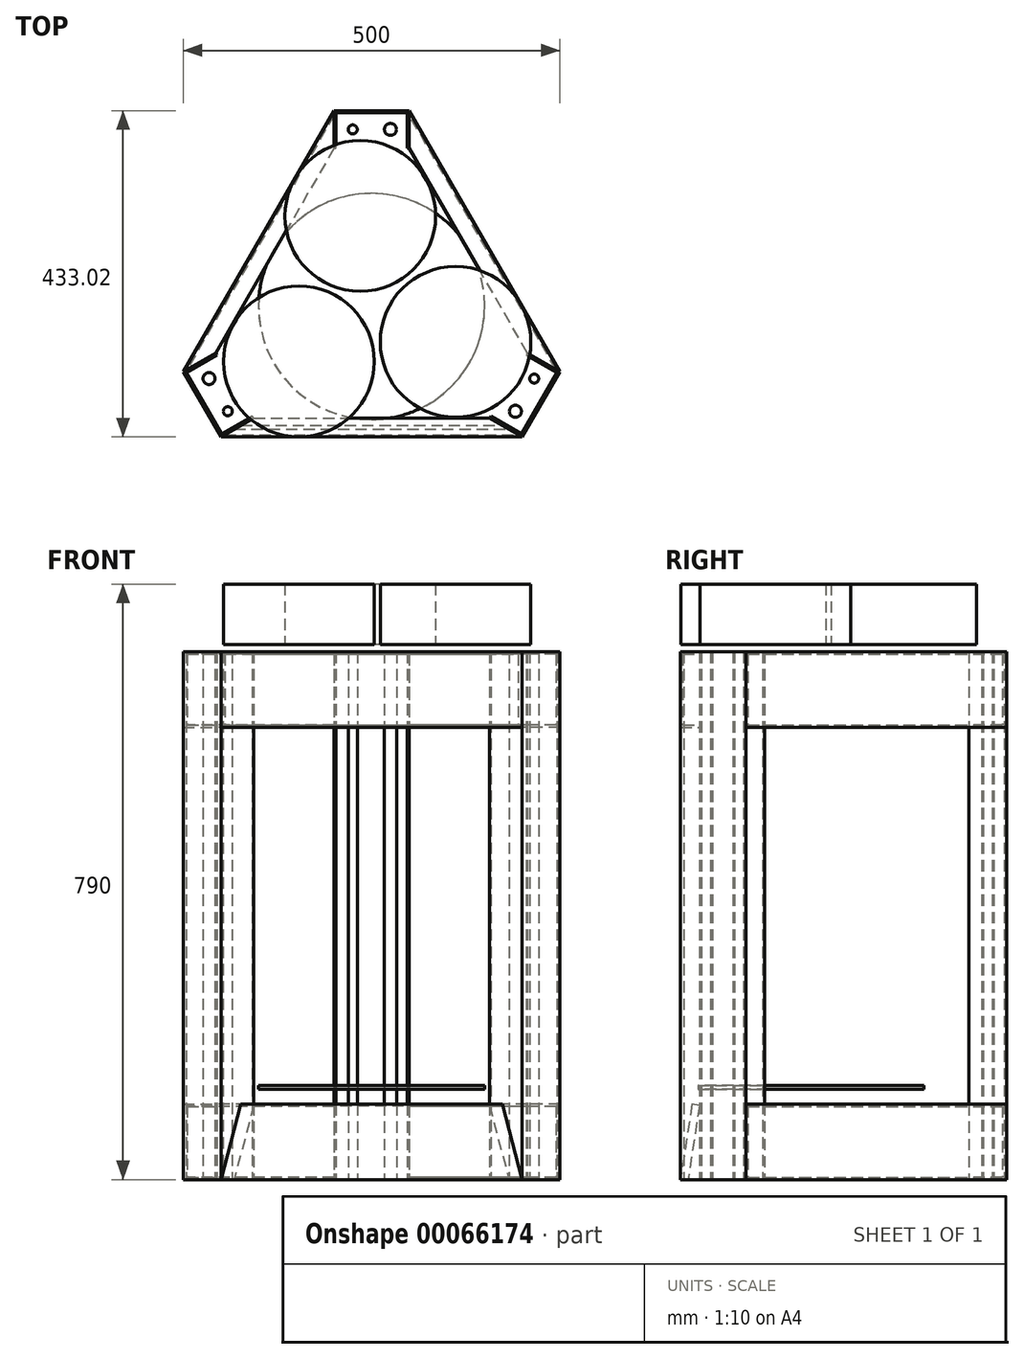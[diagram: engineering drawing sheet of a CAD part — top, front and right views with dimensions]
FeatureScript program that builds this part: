
annotation { "Feature Type Name" : "Feature", "Feature Type Description" : "" }
export const myFeature = defineFeature(function(context is Context, id is Id, definition is map)
    precondition{}
    {
        {
            var Q0;
            Q0=qCreatedBy(makeId("Top.planeOp"),FACE);
            var sketch = newSketch(context, id + "F0", { "sketchPlane" : qUnion([Q0])});
            skLineSegment(sketch, "E0.bottom", {"start": v(-50, 209.8) * mm, "end": v(50, 209.8) * mm});
            skLineSegment(sketch, "E0.top", {"start": v(-50, 259.8) * mm, "end": v(50, 259.8) * mm});
            skLineSegment(sketch, "E0.left", {"start": v(-50, 209.8) * mm, "end": v(-50, 259.8) * mm});
            skLineSegment(sketch, "E0.right", {"start": v(50, 209.8) * mm, "end": v(50, 259.8) * mm});
            skPoint(sketch, "E0.middle", {"position": v(0, 234.8) * mm});
            skLineSegment(sketch, "E1.0", {"start": v(47, 209.8) * mm, "end": v(47, 256.8) * mm});
            skLineSegment(sketch, "E1.1", {"start": v(-47, 256.8) * mm, "end": v(47, 256.8) * mm});
            skLineSegment(sketch, "E1.2", {"start": v(-47, 209.8) * mm, "end": v(-47, 256.8) * mm});
            skLineSegment(sketch, "E2.1.0", {"start": v(-198.9, -169.1) * mm, "end": v(-245.9, -87.7) * mm});
            skLineSegment(sketch, "E2.1.1", {"start": v(-200, -173.2) * mm, "end": v(-250, -86.6) * mm});
            skLineSegment(sketch, "E2.1.2", {"start": v(-156.7, -148.2) * mm, "end": v(-200, -173.2) * mm});
            skLineSegment(sketch, "E2.1.3", {"start": v(-158.2, -145.6) * mm, "end": v(-198.9, -169.1) * mm});
            skLineSegment(sketch, "E2.1.4", {"start": v(-205.2, -64.2) * mm, "end": v(-245.9, -87.7) * mm});
            skLineSegment(sketch, "E2.1.5", {"start": v(-206.7, -61.6) * mm, "end": v(-250, -86.6) * mm});
            skLineSegment(sketch, "E2.1.6", {"start": v(-156.7, -148.2) * mm, "end": v(-206.7, -61.6) * mm});
            skLineSegment(sketch, "E2.2.0", {"start": v(245.9, -87.7) * mm, "end": v(198.9, -169.1) * mm});
            skLineSegment(sketch, "E2.2.1", {"start": v(250, -86.6) * mm, "end": v(200, -173.2) * mm});
            skLineSegment(sketch, "E2.2.2", {"start": v(206.7, -61.6) * mm, "end": v(250, -86.6) * mm});
            skLineSegment(sketch, "E2.2.3", {"start": v(205.2, -64.2) * mm, "end": v(245.9, -87.7) * mm});
            skLineSegment(sketch, "E2.2.4", {"start": v(158.2, -145.6) * mm, "end": v(198.9, -169.1) * mm});
            skLineSegment(sketch, "E2.2.5", {"start": v(156.7, -148.2) * mm, "end": v(200, -173.2) * mm});
            skLineSegment(sketch, "E2.2.6", {"start": v(206.7, -61.6) * mm, "end": v(156.7, -148.2) * mm});
            skPoint(sketch, "E2.center", {"position": v(0, 0) * mm});
            skCircle(sketch, "E3", {"center": v(25, 234.8) * mm, "radius": 8 * mm});
            skCircle(sketch, "E4", {"center": v(-25, 234.8) * mm, "radius": 6 * mm});
            skCircle(sketch, "E5.1.0", {"center": v(-190.85, -139.05) * mm, "radius": 6 * mm});
            skCircle(sketch, "E5.1.1", {"center": v(-215.85, -95.75) * mm, "radius": 8 * mm});
            skCircle(sketch, "E5.2.0", {"center": v(215.85, -95.75) * mm, "radius": 6 * mm});
            skCircle(sketch, "E5.2.1", {"center": v(190.85, -139.05) * mm, "radius": 8 * mm});
            skSolve(sketch);
        }
        {
            var Q0;
            Q0=makeQuery(id+"F0.imprint","IMPRINT",FACE,{"disambiguationData":[TD([[makeQuery(id+"F0.imprint","IMPRINT",EDGE,{"derivedFrom":sQuery(id+"F0.wireOp",EDGE,"E0.top")}),-1.0]])]});
            var Q1;
            Q1=makeQuery(id+"F0.imprint","IMPRINT",FACE,{"disambiguationData":[TD([[makeQuery(id+"F0.imprint","IMPRINT",EDGE,{"derivedFrom":sQuery(id+"F0.wireOp",EDGE,"E2.1.0")}),1.0]])]});
            var Q2;
            Q2=makeQuery(id+"F0.imprint","IMPRINT",FACE,{"disambiguationData":[TD([[makeQuery(id+"F0.imprint","IMPRINT",EDGE,{"derivedFrom":sQuery(id+"F0.wireOp",EDGE,"E2.2.0")}),1.0]])]});
            var Q3;
            Q3=makeQuery(id+"F0.imprint","IMPRINT",FACE,{"disambiguationData":[TD([[makeQuery(id+"F0.imprint","IMPRINT",EDGE,{"derivedFrom":sQuery(id+"F0.wireOp",EDGE,"E4")}),1.0]])]});
            var Q4;
            Q4=makeQuery(id+"F0.imprint","IMPRINT",FACE,{"disambiguationData":[TD([[makeQuery(id+"F0.imprint","IMPRINT",EDGE,{"derivedFrom":sQuery(id+"F0.wireOp",EDGE,"E3")}),1.0]])]});
            var Q5;
            Q5=makeQuery(id+"F0.imprint","IMPRINT",FACE,{"disambiguationData":[TD([[makeQuery(id+"F0.imprint","IMPRINT",EDGE,{"derivedFrom":sQuery(id+"F0.wireOp",EDGE,"E5.1.1")}),1.0]])]});
            var Q6;
            Q6=makeQuery(id+"F0.imprint","IMPRINT",FACE,{"disambiguationData":[TD([[makeQuery(id+"F0.imprint","IMPRINT",EDGE,{"derivedFrom":sQuery(id+"F0.wireOp",EDGE,"E5.1.0")}),1.0]])]});
            var Q7;
            Q7=makeQuery(id+"F0.imprint","IMPRINT",FACE,{"disambiguationData":[TD([[makeQuery(id+"F0.imprint","IMPRINT",EDGE,{"derivedFrom":sQuery(id+"F0.wireOp",EDGE,"E5.2.1")}),1.0]])]});
            var Q8;
            Q8=makeQuery(id+"F0.imprint","IMPRINT",FACE,{"disambiguationData":[TD([[makeQuery(id+"F0.imprint","IMPRINT",EDGE,{"derivedFrom":sQuery(id+"F0.wireOp",EDGE,"E5.2.0")}),1.0]])]});
            extrude(context, id + "F1", {"entities" : qUnion([Q0, Q1, Q2, Q3, Q4, Q5, Q6, Q7, Q8]), "depth" : 700 * mm, "offsetDistance" : 25 * mm});
        }
        {
            var Q0;
            Q0=qCreatedBy(makeId("Right.planeOp"),FACE);
            var sketch = newSketch(context, id + "F2", { "sketchPlane" : qUnion([Q0])});
            skLineSegment(sketch, "E6.bottom", {"start": v(-148.2, 0) * mm, "end": v(-173.2, 0) * mm});
            skLineSegment(sketch, "E6.top", {"start": v(-148.2, 100) * mm, "end": v(-173.2, 100) * mm});
            skLineSegment(sketch, "E6.left", {"start": v(-148.2, 0) * mm, "end": v(-148.2, 100) * mm});
            skLineSegment(sketch, "E6.right", {"start": v(-173.2, 0) * mm, "end": v(-173.2, 100) * mm});
            skPoint(sketch, "E6.middle", {"position": v(-160.7, 50) * mm});
            skLineSegment(sketch, "E7.0", {"start": v(-148.2, 3) * mm, "end": v(-170.2, 3) * mm});
            skLineSegment(sketch, "E7.1", {"start": v(-170.2, 3) * mm, "end": v(-170.2, 97) * mm});
            skLineSegment(sketch, "E7.2", {"start": v(-148.2, 97) * mm, "end": v(-170.2, 97) * mm});
            skLineSegment(sketch, "E8", {"start": v(0, 0) * mm, "end": v(0, 219.6) * mm, "construction": true});
            skSolve(sketch);
        }
        {
            var Q0;
            {var subQ3=sQuery(id+"F2.wireOp",EDGE,"E6.bottom");Q0=makeQuery(id+"F2.imprint","IMPRINT",FACE,{"disambiguationData":[TD([[makeQuery(id+"F2.imprint","IMPRINT",EDGE,{"derivedFrom":subQ3}),-1.0]])]});}
            var Q1;
            Q1=makeQuery(id+"F1.opExtrude","SWEPT_FACE",FACE,{"disambiguationData":[OSD([sQuery(id+"F0.wireOp",EDGE,"E2.1.2")])]});
            var Q2;
            Q2=makeQuery(id+"F1.opExtrude","SWEPT_FACE",FACE,{"disambiguationData":[OSD([sQuery(id+"F0.wireOp",EDGE,"E2.2.5")])]});
            extrude(context, id + "F3", {"entities" : qUnion([Q0]), "endBound" : BoundingType.UP_TO_SURFACE, "oppositeDirection" : true, "depth" : 25 * mm, "endBoundEntityFace" : qUnion([Q1]), "offsetDistance" : 25 * mm, "hasSecondDirection" : true, "secondDirectionBound" : SecondDirectionBoundingType.UP_TO_SURFACE, "secondDirectionOppositeDirection" : false, "secondDirectionDepth" : 25 * mm, "secondDirectionBoundEntityFace" : qUnion([Q2])});
        }
        {
            var Q0;
            Q0=makeQuery(id+"F3.opExtrude","SWEPT_BODY",BODY,{"disambiguationData":[OSD([sQuery(id+"F2.wireOp",EDGE,"E6.bottom"),sQuery(id+"F2.wireOp",EDGE,"E6.top"),sQuery(id+"F2.wireOp",EDGE,"E6.left"),sQuery(id+"F2.wireOp",EDGE,"E6.right"),sQuery(id+"F2.wireOp",EDGE,"E7.0"),sQuery(id+"F2.wireOp",EDGE,"E7.1"),sQuery(id+"F2.wireOp",EDGE,"E7.2")])]});
            var Q1;
            Q1=sQuery(id+"F2.wireOp",EDGE,"E8");
            circularPattern(context, id + "F4", {"entities" : qUnion([Q0]), "axis" : qUnion([Q1]), "angle" : 360 * degree, "instanceCount" : 3, "equalSpace" : true});
        }
        {
            var Q0;
            Q0=makeQuery(id+"F4.opPattern","COPY",BODY,{"derivedFrom":makeQuery(id+"F3.opExtrude","SWEPT_BODY",BODY,{"disambiguationData":[OSD([sQuery(id+"F2.wireOp",EDGE,"E6.bottom"),sQuery(id+"F2.wireOp",EDGE,"E6.top"),sQuery(id+"F2.wireOp",EDGE,"E6.left"),sQuery(id+"F2.wireOp",EDGE,"E6.right"),sQuery(id+"F2.wireOp",EDGE,"E7.0"),sQuery(id+"F2.wireOp",EDGE,"E7.1"),sQuery(id+"F2.wireOp",EDGE,"E7.2")])]}),"instanceName":"2"});
            var Q1;
            Q1=makeQuery(id+"F4.opPattern","COPY",BODY,{"derivedFrom":makeQuery(id+"F3.opExtrude","SWEPT_BODY",BODY,{"disambiguationData":[OSD([sQuery(id+"F2.wireOp",EDGE,"E6.bottom"),sQuery(id+"F2.wireOp",EDGE,"E6.top"),sQuery(id+"F2.wireOp",EDGE,"E6.left"),sQuery(id+"F2.wireOp",EDGE,"E6.right"),sQuery(id+"F2.wireOp",EDGE,"E7.0"),sQuery(id+"F2.wireOp",EDGE,"E7.1"),sQuery(id+"F2.wireOp",EDGE,"E7.2")])]}),"instanceName":"1"});
            transform(context, id + "F5", {"entities" : qUnion([Q0, Q1]), "transformType" : TransformType.TRANSLATION_3D, "dx" : 0 * mm, "dy" : 0 * mm, "dz" : 600 * mm, "makeCopy" : true});
        }
        {
            var Q0;
            Q0=makeQuery(id+"F3.opExtrude","SWEPT_BODY",BODY,{"disambiguationData":[OSD([sQuery(id+"F2.wireOp",EDGE,"E6.bottom"),sQuery(id+"F2.wireOp",EDGE,"E6.top"),sQuery(id+"F2.wireOp",EDGE,"E6.left"),sQuery(id+"F2.wireOp",EDGE,"E6.right"),sQuery(id+"F2.wireOp",EDGE,"E7.0"),sQuery(id+"F2.wireOp",EDGE,"E7.1"),sQuery(id+"F2.wireOp",EDGE,"E7.2")])]});
            transform(context, id + "F6", {"entities" : qUnion([Q0]), "transformType" : TransformType.TRANSLATION_3D, "dx" : 0 * mm, "dy" : 0 * mm, "dz" : 600 * mm, "makeCopy" : false});
        }
        {
            var Q0;
            Q0=qCreatedBy(makeId("Top.planeOp"),FACE);
            cPlane(context, id + "F7", {"entities" : qUnion([Q0]), "cplaneType" : CPlaneType.OFFSET, "offset" : 120 * mm, "width" : 150 * mm, "height" : 150 * mm});
        }
        {
            var Q0;
            Q0=qCreatedBy(id+"F7.planeOp",FACE);
            var sketch = newSketch(context, id + "F8", { "sketchPlane" : qUnion([Q0])});
            skCircle(sketch, "E9", {"center": v(0, 0) * mm, "radius": 150 * mm});
            skSolve(sketch);
        }
        {
            var Q0;
            Q0 = qSketchRegion(id + "F8", true);
            extrude(context, id + "F9", {"entities" : qUnion([Q0]), "depth" : 5 * mm, "offsetDistance" : 25 * mm});
        }
        {
            var Q0;
            Q0=qCreatedBy(makeId("Top.planeOp"),FACE);
            cPlane(context, id + "F10", {"entities" : qUnion([Q0]), "cplaneType" : CPlaneType.OFFSET, "offset" : 750 * mm, "width" : 150 * mm, "height" : 150 * mm});
        }
        {
            var Q0;
            Q0=qCreatedBy(id+"F10.planeOp",FACE);
            var sketch = newSketch(context, id + "F11", { "sketchPlane" : qUnion([Q0])});
            skCircle(sketch, "E10", {"center": v(-15, 120) * mm, "radius": 100 * mm});
            skCircle(sketch, "E11.1.0", {"center": v(-96.42, -73) * mm, "radius": 100 * mm});
            skCircle(sketch, "E11.2.0", {"center": v(111.42, -47) * mm, "radius": 100 * mm});
            skPoint(sketch, "E11.center", {"position": v(0, 0) * mm});
            skSolve(sketch);
        }
        {
            var Q0;
            Q0 = qSketchRegion(id + "F11", true);
            extrude(context, id + "F12", {"entities" : qUnion([Q0]), "endBound" : BoundingType.SYMMETRIC, "depth" : 80 * mm, "offsetDistance" : 25 * mm});
        }
        {
            var Q0;
            Q0=qCreatedBy(makeId("Right.planeOp"),FACE);
            var sketch = newSketch(context, id + "F13", { "sketchPlane" : qUnion([Q0])});
            skLineSegment(sketch, "E12", {"start": v(-173.2, 0) * mm, "end": v(-157.98, 100) * mm});
            skLineSegment(sketch, "E13", {"start": v(-163.09, 0) * mm, "end": v(-173.2, 0) * mm});
            skLineSegment(sketch, "E14", {"start": v(-163.09, 0) * mm, "end": v(-148.09, 98.5) * mm});
            skLineSegment(sketch, "E15", {"start": v(-157.98, 100) * mm, "end": v(-148.09, 98.5) * mm});
            skSolve(sketch);
        }
        {
            var Q0;
            Q0 = qSketchRegion(id + "F13", true);
            var Q1;
            Q1=makeQuery(id+"F1.opExtrude","SWEPT_FACE",FACE,{"disambiguationData":[OSD([sQuery(id+"F0.wireOp",EDGE,"E2.1.2")])]});
            var Q2;
            Q2=makeQuery(id+"F1.opExtrude","SWEPT_FACE",FACE,{"disambiguationData":[OSD([sQuery(id+"F0.wireOp",EDGE,"E2.2.5")])]});
            extrude(context, id + "F14", {"entities" : qUnion([Q0]), "endBound" : BoundingType.UP_TO_SURFACE, "oppositeDirection" : true, "depth" : 25 * mm, "endBoundEntityFace" : qUnion([Q1]), "offsetDistance" : 25 * mm, "hasSecondDirection" : true, "secondDirectionBound" : SecondDirectionBoundingType.UP_TO_SURFACE, "secondDirectionOppositeDirection" : false, "secondDirectionDepth" : 25 * mm, "secondDirectionBoundEntityFace" : qUnion([Q2])});
        }
    });
